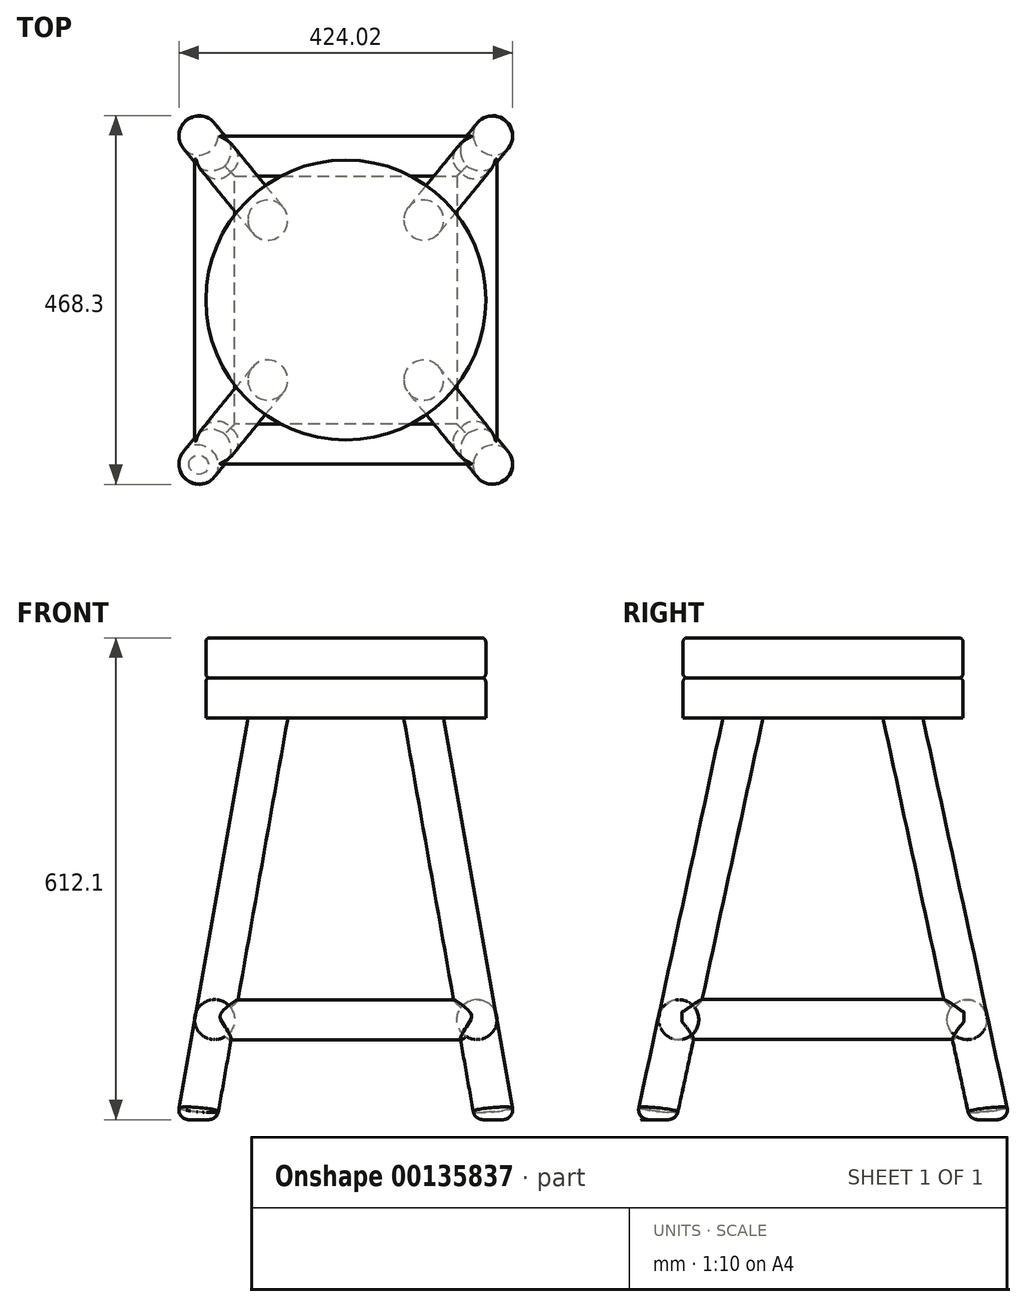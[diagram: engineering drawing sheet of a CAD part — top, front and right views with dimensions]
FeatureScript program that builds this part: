
annotation { "Feature Type Name" : "Feature", "Feature Type Description" : "" }
export const myFeature = defineFeature(function(context is Context, id is Id, definition is map)
    precondition{}
    {
        {
            var Q0;
            Q0=qCreatedBy(makeId("Top.planeOp"),FACE);
            var sketch = newSketch(context, id + "F0", { "sketchPlane" : qUnion([Q0])});
            skCircle(sketch, "E0", {"center": v(0, 0) * mm, "radius": 177.8 * mm});
            skSolve(sketch);
        }
        {
            var Q0;
            Q0=makeQuery(id+"F0.imprint","IMPRINT",FACE,{"disambiguationData":[TD([[makeQuery(id+"F0.imprint","IMPRINT",EDGE,{"derivedFrom":sQuery(id+"F0.wireOp",EDGE,"E0")}),1.0]])]});
            extrude(context, id + "F1", {"entities" : qUnion([Q0]), "endBound" : BoundingType.SYMMETRIC, "depth" : 50.8 * mm});
        }
        {
            var Q0;
            Q0=makeQuery(id+"F1.opExtrude","CAP_FACE",FACE,{"disambiguationData":[OSD([sQuery(id+"F0.wireOp",EDGE,"E0")])],"isStart":true});
            var sketch = newSketch(context, id + "F2", { "sketchPlane" : qUnion([Q0])});
            skLineSegment(sketch, "E1.bottom", {"start": v(-124.43, 127) * mm, "end": v(124.43, 127) * mm});
            skLineSegment(sketch, "E1.top", {"start": v(-124.43, -127) * mm, "end": v(124.43, -127) * mm});
            skLineSegment(sketch, "E1.left", {"start": v(-124.43, 127) * mm, "end": v(-124.43, -127) * mm});
            skLineSegment(sketch, "E1.right", {"start": v(124.43, 127) * mm, "end": v(124.43, -127) * mm});
            skCircle(sketch, "E2", {"center": v(-99.03, 101.6) * mm, "radius": 25.4 * mm});
            skCircle(sketch, "E3", {"center": v(99.03, 101.6) * mm, "radius": 25.4 * mm});
            skCircle(sketch, "E4", {"center": v(99.03, -101.6) * mm, "radius": 25.4 * mm});
            skCircle(sketch, "E5", {"center": v(-99.03, -101.6) * mm, "radius": 25.4 * mm});
            skPoint(sketch, "E6.endSnap0", {"position": v(-124.43, 0) * mm});
            skPoint(sketch, "E7.endSnap0", {"position": v(124.43, 0) * mm});
            skLineSegment(sketch, "E8", {"start": v(99.03, 101.6) * mm, "end": v(99.03, -101.6) * mm, "construction": true});
            skLineSegment(sketch, "E9", {"start": v(-99.03, 101.6) * mm, "end": v(-99.03, -101.6) * mm, "construction": true});
            skLineSegment(sketch, "E10", {"start": v(99.03, 101.6) * mm, "end": v(-99.03, 101.6) * mm, "construction": true});
            skLineSegment(sketch, "E11", {"start": v(99.03, -101.6) * mm, "end": v(-99.03, -101.6) * mm, "construction": true});
            skSolve(sketch);
        }
        {
            var Q0;
            Q0=sQuery(id+"F2.wireOp",EDGE,"E8");
            cPlane(context, id + "F3", {"entities" : qUnion([Q0]), "cplaneType" : CPlaneType.LINE_ANGLE, "offset" : 25.4 * mm, "angle" : 80 * degree, "width" : 152.4 * mm, "height" : 152.4 * mm});
        }
        {
            var Q0;
            Q0=sQuery(id+"F2.wireOp",EDGE,"E9");
            cPlane(context, id + "F4", {"entities" : qUnion([Q0]), "cplaneType" : CPlaneType.LINE_ANGLE, "offset" : 25.4 * mm, "angle" : 100 * degree, "width" : 152.4 * mm, "height" : 152.4 * mm});
        }
        {
            var Q0;
            Q0=qCreatedBy(makeId("Front.planeOp"),FACE);
            var sketch = newSketch(context, id + "F5", { "sketchPlane" : qUnion([Q0])});
            skLineSegment(sketch, "E12", {"start": v(0, 0) * mm, "end": v(0, -533.4) * mm, "construction": true});
            skLineSegment(sketch, "E13", {"start": v(203.2, -533.4) * mm, "end": v(-203.2, -533.4) * mm, "construction": true});
            skLineSegment(sketch, "E14", {"start": v(-177.8, -381) * mm, "end": v(177.8, -381) * mm, "construction": true});
            skPoint(sketch, "E15", {"position": v(0, -381) * mm});
            skSolve(sketch);
        }
        {
            var Q0;
            Q0=qCreatedBy(id+"F3.planeOp",FACE);
            var sketch = newSketch(context, id + "F6", { "sketchPlane" : qUnion([Q0])});
            skLineSegment(sketch, "E16", {"start": v(-101.6, -42.21) * mm, "end": v(-101.6, -560.58) * mm, "construction": true});
            skLineSegment(sketch, "E17", {"start": v(-101.6, -42.21) * mm, "end": v(-211.78, -560.58) * mm});
            skLineSegment(sketch, "E18", {"start": v(-101.6, -560.58) * mm, "end": v(-211.78, -560.58) * mm, "construction": true});
            skLineSegment(sketch, "E19", {"start": v(0, -46.62) * mm, "end": v(0, -560.58) * mm, "construction": true});
            skLineSegment(sketch, "E20", {"start": v(101.6, -42.21) * mm, "end": v(101.6, -560.58) * mm, "construction": true});
            skLineSegment(sketch, "E21", {"start": v(101.6, -560.58) * mm, "end": v(-101.6, -560.58) * mm, "construction": true});
            skLineSegment(sketch, "E22", {"start": v(101.6, -42.21) * mm, "end": v(211.78, -560.58) * mm});
            skLineSegment(sketch, "E23", {"start": v(211.78, -560.58) * mm, "end": v(101.6, -560.58) * mm, "construction": true});
            skLineSegment(sketch, "E24", {"start": v(-178.94, -406.09) * mm, "end": v(178.94, -406.09) * mm});
            skLineSegment(sketch, "E25", {"start": v(-184.34, -431.49) * mm, "end": v(184.34, -431.49) * mm});
            skSolve(sketch);
        }
        {
            var Q0;
            Q0=qCreatedBy(id+"F4.planeOp",FACE);
            var sketch = newSketch(context, id + "F7", { "sketchPlane" : qUnion([Q0])});
            skLineSegment(sketch, "E26", {"start": v(101.6, -42.21) * mm, "end": v(211.78, -560.58) * mm});
            skLineSegment(sketch, "E27", {"start": v(-101.6, -42.21) * mm, "end": v(-211.78, -560.58) * mm});
            skLineSegment(sketch, "E28", {"start": v(211.78, -560.58) * mm, "end": v(-211.78, -560.58) * mm, "construction": true});
            skLineSegment(sketch, "E29", {"start": v(101.6, -560.58) * mm, "end": v(101.6, -42.21) * mm, "construction": true});
            skLineSegment(sketch, "E30", {"start": v(0, -560.58) * mm, "end": v(0, -46.62) * mm, "construction": true});
            skLineSegment(sketch, "E31", {"start": v(-101.6, -560.58) * mm, "end": v(-101.6, -42.21) * mm, "construction": true});
            skLineSegment(sketch, "E32", {"start": v(178.94, -406.09) * mm, "end": v(-178.94, -406.09) * mm});
            skLineSegment(sketch, "E33", {"start": v(184.34, -431.49) * mm, "end": v(-184.34, -431.49) * mm});
            skSolve(sketch);
        }
        {
            var Q0;
            Q0=sQuery(id+"F2.wireOp",EDGE,"E10");
            cPlane(context, id + "F8", {"entities" : qUnion([Q0]), "cplaneType" : CPlaneType.LINE_ANGLE, "offset" : 25.4 * mm, "angle" : 12 * degree, "width" : 152.4 * mm, "height" : 152.4 * mm});
        }
        {
            var Q0;
            Q0=sQuery(id+"F2.wireOp",EDGE,"E11");
            cPlane(context, id + "F9", {"entities" : qUnion([Q0]), "cplaneType" : CPlaneType.LINE_ANGLE, "offset" : 25.4 * mm, "angle" : 168 * degree, "width" : 152.4 * mm, "height" : 152.4 * mm});
        }
        {
            var Q0;
            Q0=qCreatedBy(id+"F9.planeOp",FACE);
            var sketch = newSketch(context, id + "F10", { "sketchPlane" : qUnion([Q0])});
            skLineSegment(sketch, "E34", {"start": v(99.03, -45.97) * mm, "end": v(189.05, -568.22) * mm, "construction": true});
            skLineSegment(sketch, "E35", {"start": v(-99.03, -45.97) * mm, "end": v(-189.05, -568.22) * mm, "construction": true});
            skLineSegment(sketch, "E36", {"start": v(-189.05, -568.22) * mm, "end": v(189.05, -568.22) * mm, "construction": true});
            skLineSegment(sketch, "E37", {"start": v(-162.22, -412.57) * mm, "end": v(162.22, -412.57) * mm});
            skLineSegment(sketch, "E38", {"start": v(-166.6, -437.97) * mm, "end": v(166.6, -437.97) * mm});
            skLineSegment(sketch, "E39", {"start": v(166.6, -437.97) * mm, "end": v(162.22, -412.57) * mm});
            skLineSegment(sketch, "E40", {"start": v(-166.6, -437.97) * mm, "end": v(-162.22, -412.57) * mm});
            skSolve(sketch);
        }
        {
            var Q0;
            Q0=qCreatedBy(id+"F8.planeOp",FACE);
            var sketch = newSketch(context, id + "F11", { "sketchPlane" : qUnion([Q0])});
            skLineSegment(sketch, "E41", {"start": v(-99.03, -45.97) * mm, "end": v(-189.05, -568.22) * mm, "construction": true});
            skLineSegment(sketch, "E42", {"start": v(99.03, -45.97) * mm, "end": v(189.05, -568.22) * mm, "construction": true});
            skLineSegment(sketch, "E43", {"start": v(-162.22, -412.57) * mm, "end": v(162.22, -412.57) * mm});
            skLineSegment(sketch, "E44", {"start": v(-166.6, -437.97) * mm, "end": v(166.6, -437.97) * mm});
            skLineSegment(sketch, "E45", {"start": v(-166.6, -437.97) * mm, "end": v(-162.22, -412.57) * mm});
            skLineSegment(sketch, "E46", {"start": v(166.6, -437.97) * mm, "end": v(162.22, -412.57) * mm});
            skSolve(sketch);
        }
        {
            var Q0;
            Q0=sQuery(id+"F5.wireOp",EDGE,"E13");
            cPlane(context, id + "F12", {"entities" : qUnion([Q0]), "cplaneType" : CPlaneType.LINE_ANGLE, "offset" : 25.4 * mm, "angle" : 90 * degree, "width" : 152.4 * mm, "height" : 152.4 * mm});
        }
        {
            var Q0;
            {var subQ0=sQuery(id+"F2.wireOp",EDGE,"E5");var subQ1=makeQuery(id+"F2.imprint","INTERSECT",VERTEX,{"derivedFrom":[sQuery(id+"F2.wireOp",EDGE,"E1.top"),subQ0]});Q0=makeQuery(id+"F2.imprint","IMPRINT",FACE,{"disambiguationData":[TD([[makeQuery(id+"F2.imprint","IMPRINT",EDGE,{"disambiguationData":[TD([[subQ1,1.0]])],"derivedFrom":subQ0}),1.0]])]});}
            var Q1;
            Q1=sQuery(id+"F7.wireOp",EDGE,"E26");
            sweep(context, id + "F13", {"operationType" : NewBodyOperationType.ADD, "profiles" : qUnion([Q0]), "path" : qUnion([Q1])});
        }
        {
            var Q0;
            {var subQ0=sQuery(id+"F2.wireOp",EDGE,"E2");var subQ1=makeQuery(id+"F2.imprint","INTERSECT",VERTEX,{"derivedFrom":[sQuery(id+"F2.wireOp",EDGE,"E1.bottom"),subQ0]});Q0=makeQuery(id+"F2.imprint","IMPRINT",FACE,{"disambiguationData":[TD([[makeQuery(id+"F2.imprint","IMPRINT",EDGE,{"disambiguationData":[TD([[subQ1,-1.0]])],"derivedFrom":subQ0}),1.0]])]});}
            var Q1;
            Q1=sQuery(id+"F7.wireOp",EDGE,"E27");
            sweep(context, id + "F14", {"operationType" : NewBodyOperationType.ADD, "profiles" : qUnion([Q0]), "path" : qUnion([Q1])});
        }
        {
            var Q0;
            {var subQ0=sQuery(id+"F2.wireOp",EDGE,"E3");var subQ1=makeQuery(id+"F2.imprint","INTERSECT",VERTEX,{"derivedFrom":[sQuery(id+"F2.wireOp",EDGE,"E1.bottom"),subQ0]});Q0=makeQuery(id+"F2.imprint","IMPRINT",FACE,{"disambiguationData":[TD([[makeQuery(id+"F2.imprint","IMPRINT",EDGE,{"disambiguationData":[TD([[subQ1,1.0]])],"derivedFrom":subQ0}),1.0]])]});}
            var Q1;
            Q1=sQuery(id+"F6.wireOp",EDGE,"E17");
            sweep(context, id + "F15", {"operationType" : NewBodyOperationType.ADD, "profiles" : qUnion([Q0]), "path" : qUnion([Q1])});
        }
        {
            var Q0;
            {var subQ0=sQuery(id+"F2.wireOp",EDGE,"E4");var subQ1=makeQuery(id+"F2.imprint","INTERSECT",VERTEX,{"derivedFrom":[sQuery(id+"F2.wireOp",EDGE,"E1.top"),subQ0]});Q0=makeQuery(id+"F2.imprint","IMPRINT",FACE,{"disambiguationData":[TD([[makeQuery(id+"F2.imprint","IMPRINT",EDGE,{"disambiguationData":[TD([[subQ1,1.0]])],"derivedFrom":subQ0}),1.0]])]});}
            var Q1;
            Q1=sQuery(id+"F6.wireOp",EDGE,"E22");
            sweep(context, id + "F16", {"operationType" : NewBodyOperationType.ADD, "profiles" : qUnion([Q0]), "path" : qUnion([Q1])});
        }
        {
            var Q0;
            {var subQ0=sQuery(id+"F6.wireOp",EDGE,"E24");Q0=makeQuery(id+"F6.imprint","IMPRINT",FACE,{"disambiguationData":[TD([[makeQuery(id+"F6.imprint","IMPRINT",EDGE,{"derivedFrom":subQ0}),-1.0]])]});}
            var Q1;
            Q1=sQuery(id+"F6.wireOp",EDGE,"E25");
            revolve(context, id + "F17", {"operationType" : NewBodyOperationType.ADD, "entities" : qUnion([Q0]), "axis" : qUnion([Q1]), "revolveType" : RevolveType.FULL});
        }
        {
            var Q0;
            Q0=makeQuery(id+"F11.imprint","IMPRINT",FACE,{"disambiguationData":[TD([[makeQuery(id+"F11.imprint","IMPRINT",EDGE,{"derivedFrom":sQuery(id+"F11.wireOp",EDGE,"E43")}),-1.0]])]});
            var Q1;
            Q1=sQuery(id+"F11.wireOp",EDGE,"E44");
            revolve(context, id + "F18", {"operationType" : NewBodyOperationType.ADD, "entities" : qUnion([Q0]), "axis" : qUnion([Q1]), "revolveType" : RevolveType.FULL});
        }
        {
            var Q0;
            Q0=makeQuery(id+"F10.imprint","IMPRINT",FACE,{"disambiguationData":[TD([[makeQuery(id+"F10.imprint","IMPRINT",EDGE,{"derivedFrom":sQuery(id+"F10.wireOp",EDGE,"E37")}),-1.0]])]});
            var Q1;
            Q1=sQuery(id+"F10.wireOp",EDGE,"E38");
            revolve(context, id + "F19", {"operationType" : NewBodyOperationType.ADD, "entities" : qUnion([Q0]), "axis" : qUnion([Q1]), "revolveType" : RevolveType.FULL});
        }
        {
            var Q0;
            {var subQ0=sQuery(id+"F7.wireOp",EDGE,"E32");Q0=makeQuery(id+"F7.imprint","IMPRINT",FACE,{"disambiguationData":[TD([[makeQuery(id+"F7.imprint","IMPRINT",EDGE,{"derivedFrom":subQ0}),1.0]])]});}
            var Q1;
            Q1=sQuery(id+"F7.wireOp",EDGE,"E33");
            revolve(context, id + "F20", {"operationType" : NewBodyOperationType.ADD, "entities" : qUnion([Q0]), "axis" : qUnion([Q1]), "revolveType" : RevolveType.FULL});
        }
        {
            var Q0;
            Q0=makeQuery(id+"F1.opExtrude","CAP_FACE",FACE,{"disambiguationData":[OSD([sQuery(id+"F0.wireOp",EDGE,"E0")])],"isStart":false});
            var sketch = newSketch(context, id + "F21", { "sketchPlane" : qUnion([Q0])});
            skCircle(sketch, "E47", {"center": v(0, 0) * mm, "radius": 177.8 * mm});
            skSolve(sketch);
        }
        {
            var Q0;
            Q0=makeQuery(id+"F21.imprint","IMPRINT",FACE,{"disambiguationData":[TD([[makeQuery(id+"F21.imprint","IMPRINT",EDGE,{"derivedFrom":sQuery(id+"F21.wireOp",EDGE,"E47")}),1.0]])]});
            extrude(context, id + "F22", {"entities" : qUnion([Q0]), "depth" : 50.8 * mm});
        }
        {
            var Q0;
            Q0=makeQuery(id+"F22.opExtrude","CAP_EDGE",EDGE,{"disambiguationData":[OSD([sQuery(id+"F21.wireOp",EDGE,"E47")])],"isStart":false});
            var Q1;
            Q1=makeQuery(id+"F1.opExtrude","CAP_EDGE",EDGE,{"disambiguationData":[OSD([sQuery(id+"F0.wireOp",EDGE,"E0")])],"isStart":false});
            fillet(context, id + "F23", {"entities" : qUnion([Q0, Q1]), "radius" : 5.08 * mm, "tangentPropagation" : true, "allowEdgeOverflow" : false});
        }
        {
            var Q0;
            Q0=makeQuery(id+"F22.opExtrude","CAP_EDGE",EDGE,{"disambiguationData":[OSD([sQuery(id+"F21.wireOp",EDGE,"E47")])],"isStart":true});
            fillet(context, id + "F24", {"entities" : qUnion([Q0]), "radius" : 5.08 * mm, "tangentPropagation" : true, "allowEdgeOverflow" : false});
        }
        {
            var Q0;
            Q0=makeQuery(id+"F14.opSweep","CAP_EDGE",EDGE,{"disambiguationData":[OSD([sQuery(id+"F2.wireOp",EDGE,"E2"),sQuery(id+"F7.wireOp",VERTEX,"E27.end")])],"isStart":false});
            var Q1;
            Q1=makeQuery(id+"F15.opSweep","CAP_EDGE",EDGE,{"disambiguationData":[OSD([sQuery(id+"F2.wireOp",EDGE,"E3"),sQuery(id+"F6.wireOp",VERTEX,"E17.end")])],"isStart":false});
            var Q2;
            Q2=makeQuery(id+"F16.opSweep","CAP_EDGE",EDGE,{"disambiguationData":[OSD([sQuery(id+"F2.wireOp",EDGE,"E4"),sQuery(id+"F6.wireOp",VERTEX,"E22.end")])],"isStart":false});
            var Q3;
            Q3=makeQuery(id+"F13.opSweep","CAP_EDGE",EDGE,{"disambiguationData":[OSD([sQuery(id+"F2.wireOp",EDGE,"E5"),sQuery(id+"F7.wireOp",VERTEX,"E26.end")])],"isStart":false});
            fillet(context, id + "F25", {"entities" : qUnion([Q0, Q1, Q2, Q3]), "radius" : 12.7 * mm, "tangentPropagation" : true, "allowEdgeOverflow" : false});
        }
    });
